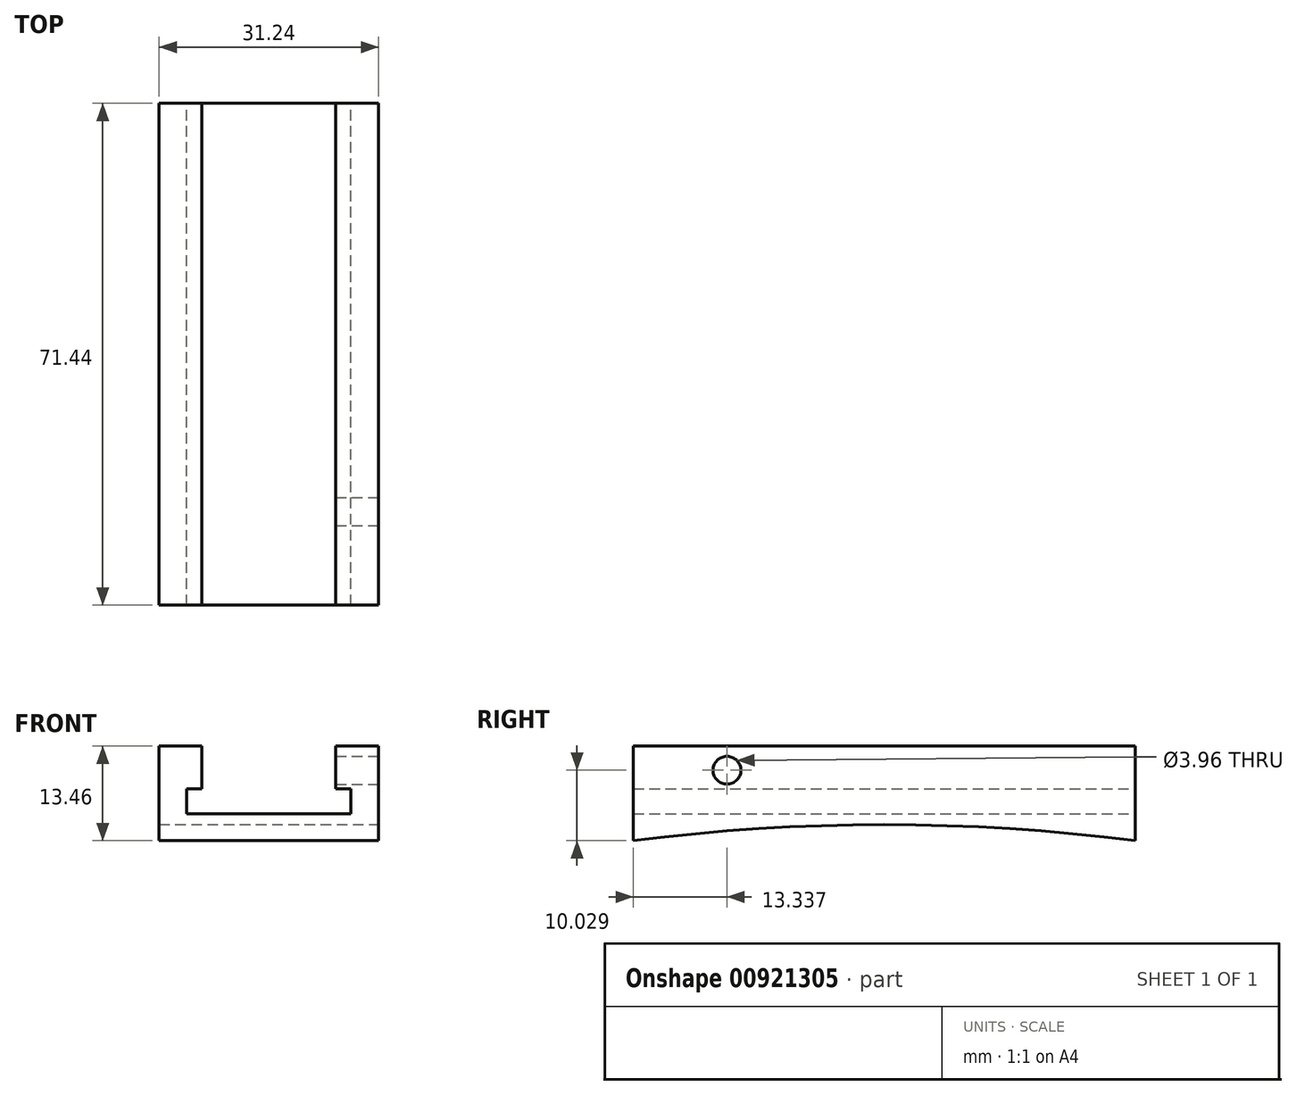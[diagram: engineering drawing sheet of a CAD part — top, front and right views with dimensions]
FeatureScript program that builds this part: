
annotation { "Feature Type Name" : "Feature", "Feature Type Description" : "" }
export const myFeature = defineFeature(function(context is Context, id is Id, definition is map)
    precondition{}
    {
        {
            var Q0;
            Q0=qCreatedBy(makeId("Front.planeOp"),FACE);
            var sketch = newSketch(context, id + "F0", { "sketchPlane" : qUnion([Q0])});
            skLineSegment(sketch, "E0", {"start": v(3.18, 12.19) * mm, "end": v(-2.91, 12.19) * mm});
            skLineSegment(sketch, "E1", {"start": v(-2.91, 12.19) * mm, "end": v(-2.91, -1.27) * mm});
            skLineSegment(sketch, "E2", {"start": v(-2.91, -1.27) * mm, "end": v(28.33, -1.27) * mm});
            skLineSegment(sketch, "E3", {"start": v(28.33, -1.27) * mm, "end": v(28.33, 12.19) * mm});
            skLineSegment(sketch, "E4", {"start": v(28.33, 12.19) * mm, "end": v(22.23, 12.19) * mm});
            skLineSegment(sketch, "E5", {"start": v(22.23, 12.19) * mm, "end": v(22.23, 6.1) * mm});
            skLineSegment(sketch, "E6", {"start": v(22.23, 6.1) * mm, "end": v(24.4, 6.1) * mm});
            skLineSegment(sketch, "E7", {"start": v(24.4, 6.1) * mm, "end": v(24.4, 2.54) * mm});
            skLineSegment(sketch, "E8", {"start": v(24.4, 2.54) * mm, "end": v(1.02, 2.54) * mm});
            skLineSegment(sketch, "E9", {"start": v(1.02, 2.54) * mm, "end": v(1.02, 6.1) * mm});
            skLineSegment(sketch, "E10", {"start": v(1.02, 6.1) * mm, "end": v(3.18, 6.1) * mm});
            skLineSegment(sketch, "E11", {"start": v(3.18, 6.1) * mm, "end": v(3.18, 12.19) * mm});
            skSolve(sketch);
        }
        {
            var Q0;
            Q0=makeQuery(id+"F0.imprint","IMPRINT",FACE,{"disambiguationData":[TD([[makeQuery(id+"F0.imprint","IMPRINT",EDGE,{"derivedFrom":sQuery(id+"F0.wireOp",EDGE,"E0")}),1.0]])]});
            extrude(context, id + "F1", {"entities" : qUnion([Q0]), "depth" : 71.44 * mm, "offsetDistance" : 25.4 * mm});
        }
        {
            var Q0;
            Q0=makeQuery(id+"F1.opExtrude","SWEPT_FACE",FACE,{"disambiguationData":[OSD([sQuery(id+"F0.wireOp",EDGE,"E3")])]});
            var sketch = newSketch(context, id + "F2", { "sketchPlane" : qUnion([Q0])});
            skCircle(sketch, "E12", {"center": v(-58.1, 8.76) * mm, "radius": 1.98 * mm});
            skSolve(sketch);
        }
        {
            var Q0;
            Q0=makeQuery(id+"F2.imprint","IMPRINT",FACE,{"disambiguationData":[TD([[makeQuery(id+"F2.imprint","IMPRINT",EDGE,{"derivedFrom":sQuery(id+"F2.wireOp",EDGE,"E12")}),1.0]])]});
            var Q1;
            Q1=sQuery(id+"F2.wireOp",EDGE,"E12");
            extrude(context, id + "F3", {"entities" : qUnion([Q0]), "operationType" : NewBodyOperationType.REMOVE, "surfaceEntities" : qUnion([Q1]), "endBound" : BoundingType.UP_TO_NEXT, "oppositeDirection" : true, "depth" : 25.4 * mm, "offsetDistance" : 25.4 * mm});
        }
        {
            var Q0;
            Q0=makeQuery(id+"F1.opExtrude","SWEPT_FACE",FACE,{"disambiguationData":[OSD([sQuery(id+"F0.wireOp",EDGE,"E3")])]});
            var sketch = newSketch(context, id + "F4", { "sketchPlane" : qUnion([Q0])});
            skLineSegment(sketch, "E13", {"start": v(-71.44, -1.27) * mm, "end": v(0, -1.27) * mm});
            skArc(sketch, "E14", {"start": v(0, -1.27) * mm, "mid": v(-35.72, 1.01) * mm, "end": v(-71.44, -1.27) * mm});
            skSolve(sketch);
        }
        {
            var Q0;
            Q0=makeQuery(id+"F4.imprint","IMPRINT",FACE,{"disambiguationData":[TD([[makeQuery(id+"F4.imprint","IMPRINT",EDGE,{"derivedFrom":sQuery(id+"F4.wireOp",EDGE,"xkWiiFVv-9acL-7Ic2-pudx-YWSvsJnFWfd3")}),1.0]])]});
            var Q1;
            Q1=makeQuery(id+"F4.imprint","IMPRINT",FACE,{"disambiguationData":[TD([[makeQuery(id+"F4.imprint","IMPRINT",EDGE,{"derivedFrom":sQuery(id+"F4.wireOp",EDGE,"E13")}),1.0]])]});
            extrude(context, id + "F5", {"entities" : qUnion([Q0, Q1]), "operationType" : NewBodyOperationType.REMOVE, "endBound" : BoundingType.THROUGH_ALL, "oppositeDirection" : true, "depth" : 25.4 * mm, "offsetDistance" : 25.4 * mm});
        }
    });
